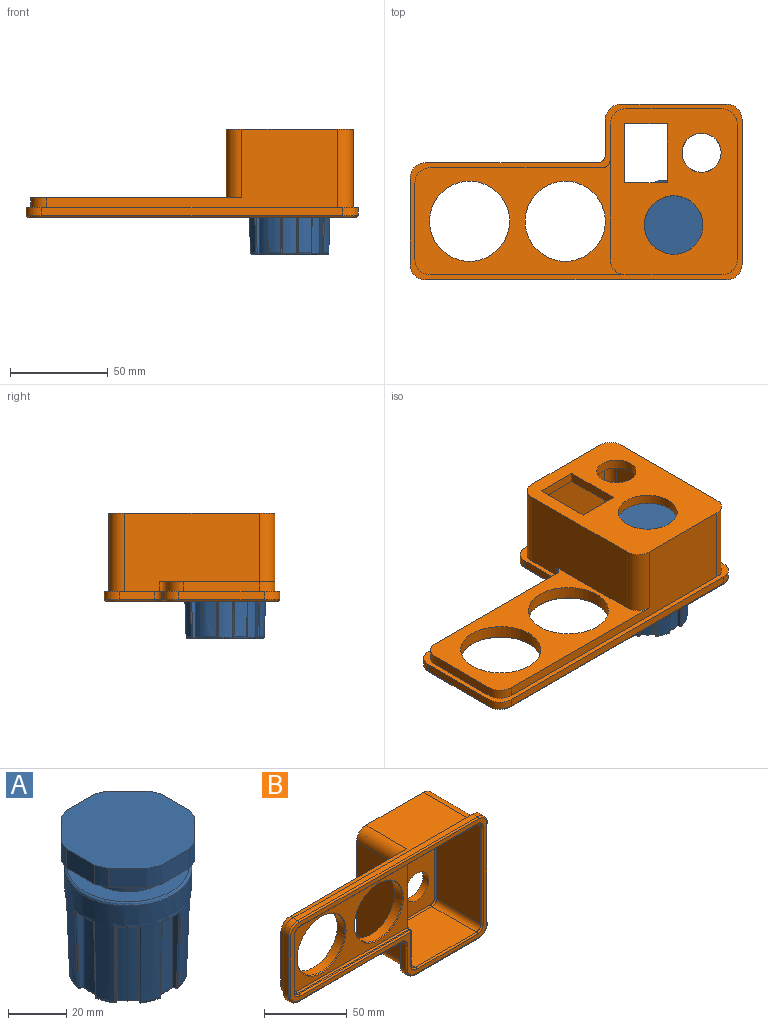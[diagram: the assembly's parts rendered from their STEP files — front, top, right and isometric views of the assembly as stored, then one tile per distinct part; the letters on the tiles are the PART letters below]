
ASSEMBLY  parts=2 mates=1
PART A: 130 faces, bbox 47.5x47.5x84 mm
  f0: cone r=22mm half-angle=2deg, axis (0,0,1), area 3146.3mm2, adj f1,f2,f3,f4,f5,f6,f7,f8
  f1: torus R=19.51mm, axis (0,0,1), area 10.6mm2, adj f0,f20,f72,f123
  f2: torus R=19.51mm, axis (0,0,1), area 10.6mm2, adj f0,f20,f67,f80
  f3: torus R=19.51mm, axis (0,0,1), area 10.6mm2, adj f0,f20,f75,f88
  f4: torus R=19.51mm, axis (0,0,1), area 10.6mm2, adj f0,f20,f83,f96
  f5: torus R=19.51mm, axis (0,0,1), area 10.6mm2, adj f0,f20,f91,f104
  f6: torus R=19.51mm, axis (0,0,1), area 10.6mm2, adj f0,f20,f99,f112
  f7: torus R=19.51mm, axis (0,0,1), area 10.6mm2, adj f0,f20,f107,f120
  f8: torus R=19.51mm, axis (0,0,1), area 10.6mm2, adj f0,f20,f115,f128
  f9: plane 46x46mm, normal (0,0,1), area 1736.1mm2, adj f10,f11,f12,f13,f14,f15,f16,f17
  f10: cylinder r=24mm len=8mm, axis (0,0,1), area 39.6mm2, adj f9,f21,f31,f32
  f11: cylinder r=24mm len=8mm, axis (0,0,1), area 39.6mm2, adj f9,f21,f25,f32
  f12: cylinder r=24mm len=8mm, axis (0,0,1), area 39.6mm2, adj f9,f21,f30,f31
  f13: cylinder r=24mm len=8mm, axis (0,0,1), area 39.6mm2, adj f9,f21,f29,f30
  f14: cylinder r=24mm len=8mm, axis (0,0,1), area 39.6mm2, adj f9,f21,f28,f29
  f15: cylinder r=24mm len=8mm, axis (0,0,1), area 39.6mm2, adj f9,f21,f27,f28
  f16: cylinder r=24mm len=8mm, axis (0,0,1), area 39.6mm2, adj f9,f21,f26,f27
  f17: cylinder r=24mm len=8mm, axis (0,0,1), area 39.6mm2, adj f9,f21,f25,f26
  f18: cylinder r=15mm len=30mm, axis (0,0,1), area 471.2mm2, adj f19,f23
  f19: plane 41.93x41.93mm, normal (0,0,1), area 673.9mm2, adj f18,f24
  f20: plane 38.06x38.06mm, normal (0,0,-1), area 1094.7mm2, adj f1,f2,f3,f4,f5,f6,f7,f8
  f21: plane 46x46mm, normal (0,0,-1), area 350.7mm2, adj f10,f11,f12,f13,f14,f15,f16,f17
  f22: cylinder r=21mm len=42mm, axis (0,0,1), area 197.9mm2, adj f21,f33
  f23: plane 40x40mm, normal (0,0,-1), area 549.8mm2, adj f18,f33
  f24: torus R=20.96mm, axis (0,0,-1), area 218mm2, adj f0,f19
  f25: plane 9.7x9.7mm, normal (0.71,-0.71,0), area 109.7mm2, adj f9,f11,f17,f21
  f26: plane 13.71x8mm, normal (0,-1,0), area 109.7mm2, adj f9,f16,f17,f21
  f27: plane 9.7x9.7mm, normal (-0.71,-0.71,0), area 109.7mm2, adj f9,f15,f16,f21
  f28: plane 13.71x8mm, normal (-1,0,0), area 109.7mm2, adj f9,f14,f15,f21
  f29: plane 9.7x9.7mm, normal (-0.71,0.71,0), area 109.7mm2, adj f9,f13,f14,f21
  f30: plane 13.71x8mm, normal (0,1,0), area 109.7mm2, adj f9,f12,f13,f21
  f31: plane 9.7x9.7mm, normal (0.71,0.71,0), area 109.7mm2, adj f9,f10,f12,f21
  f32: plane 13.71x8mm, normal (1,0,0), area 109.7mm2, adj f9,f10,f11,f21
  f33: cone r=21mm half-angle=45deg, axis (0,0,1), area 182.2mm2, adj f22,f23
  f34: plane 32.5x2.18mm, normal (-0.56,-0.83,0), area 66.7mm2, adj f36,f37,f122,f123,f125
  f35: plane 32.5x2.18mm, normal (0.83,0.56,0), area 66.7mm2, adj f36,f37,f126,f128,f129
  f36: cylinder r=18.5mm len=32.5mm, axis (0,0,-1), area 236.1mm2, adj f34,f35,f37,f127
  f37: plane 7.3x7.3mm, normal (0,0,-1), area 20.6mm2, adj f34,f35,f36,f122,f124,f126
  f38: plane 32.5x2.57mm, normal (-0.98,-0.2,0), area 66.7mm2, adj f40,f41,f114,f115,f117
  f39: plane 32.5x2.57mm, normal (0.98,-0.2,0), area 66.7mm2, adj f40,f41,f118,f120,f121
  f40: cylinder r=18.5mm len=32.5mm, axis (0,0,-1), area 236.1mm2, adj f38,f39,f41,f119
  f41: plane 8.25x3mm, normal (0,0,-1), area 20.6mm2, adj f38,f39,f40,f114,f116,f118
  f42: plane 32.5x2.18mm, normal (-0.83,0.56,0), area 66.7mm2, adj f44,f45,f106,f107,f109
  f43: plane 32.5x2.18mm, normal (0.56,-0.83,0), area 66.7mm2, adj f44,f45,f110,f112,f113
  f44: cylinder r=18.5mm len=32.5mm, axis (0,0,-1), area 236.1mm2, adj f42,f43,f45,f111
  f45: plane 7.3x7.3mm, normal (0,0,-1), area 20.6mm2, adj f42,f43,f44,f106,f108,f110
  f46: plane 32.5x2.57mm, normal (-0.2,0.98,0), area 66.7mm2, adj f48,f49,f98,f99,f101
  f47: plane 32.5x2.57mm, normal (-0.2,-0.98,0), area 66.7mm2, adj f48,f49,f102,f104,f105
  f48: cylinder r=18.5mm len=32.5mm, axis (0,0,-1), area 236.1mm2, adj f46,f47,f49,f103
  f49: plane 8.25x3mm, normal (0,0,-1), area 20.6mm2, adj f46,f47,f48,f98,f100,f102
  f50: plane 32.5x2.18mm, normal (0.56,0.83,0), area 66.7mm2, adj f52,f53,f90,f91,f93
  f51: plane 32.5x2.18mm, normal (-0.83,-0.56,0), area 66.7mm2, adj f52,f53,f94,f96,f97
  f52: cylinder r=18.5mm len=32.5mm, axis (0,0,-1), area 236.1mm2, adj f50,f51,f53,f95
  f53: plane 7.3x7.3mm, normal (0,0,-1), area 20.6mm2, adj f50,f51,f52,f90,f92,f94
  f54: plane 32.5x2.57mm, normal (0.98,0.2,0), area 66.7mm2, adj f56,f57,f82,f83,f85
  f55: plane 32.5x2.57mm, normal (-0.98,0.2,0), area 66.7mm2, adj f56,f57,f86,f88,f89
  f56: cylinder r=18.5mm len=32.5mm, axis (0,0,-1), area 236.1mm2, adj f54,f55,f57,f87
  f57: plane 8.25x3mm, normal (0,0,-1), area 20.6mm2, adj f54,f55,f56,f82,f84,f86
  f58: plane 32.5x2.18mm, normal (0.83,-0.56,0), area 66.7mm2, adj f60,f61,f74,f75,f77
  f59: plane 32.5x2.18mm, normal (-0.56,0.83,0), area 66.7mm2, adj f60,f61,f78,f80,f81
  f60: cylinder r=18.5mm len=32.5mm, axis (0,0,-1), area 236.1mm2, adj f58,f59,f61,f79
  f61: plane 7.3x7.3mm, normal (0,0,-1), area 20.6mm2, adj f58,f59,f60,f74,f76,f78
  f62: plane 8.25x3mm, normal (0,0,-1), area 20.6mm2, adj f63,f64,f65,f66,f68,f70
  f63: plane 32.5x2.57mm, normal (0.2,0.98,0), area 66.7mm2, adj f62,f64,f70,f72,f73
  f64: cylinder r=18.5mm len=32.5mm, axis (0,0,-1), area 236.1mm2, adj f62,f63,f65,f71
  f65: plane 32.5x2.57mm, normal (0.2,-0.98,0), area 66.7mm2, adj f62,f64,f66,f67,f69
  f66: bspline ~64.42x2.71mm, area 25.7mm2, adj f0,f62,f65,f67,f68
  f67: bspline ~1.19x1.15mm, area 1mm2, adj f2,f65,f66,f69
  f68: torus R=21.14mm, axis (0,0,-1), area 6.9mm2, adj f0,f62,f66,f70
  f69: cylinder r=0.5mm len=1.58mm, axis (0.98,0.2,0), area 1mm2, adj f20,f65,f67,f71
  f70: bspline ~64.42x2.71mm, area 25.7mm2, adj f0,f62,f63,f68,f72
  f71: torus R=18mm, axis (0,0,1), area 6mm2, adj f20,f64,f69,f73
  f72: bspline ~1.31x1.19mm, area 1mm2, adj f1,f63,f70,f73
  f73: cylinder r=0.5mm len=1.58mm, axis (-0.98,0.2,0), area 1mm2, adj f20,f63,f71,f72
  f74: bspline ~64.42x2.57mm, area 25.7mm2, adj f0,f58,f61,f75,f76
  f75: bspline ~1.3x1.19mm, area 1mm2, adj f3,f58,f74,f77
  f76: torus R=21.14mm, axis (0,0,-1), area 6.9mm2, adj f0,f61,f74,f78
  f77: cylinder r=0.5mm len=1.53mm, axis (0.56,0.83,0), area 1mm2, adj f20,f58,f75,f79
  f78: bspline ~64.42x2.57mm, area 25.7mm2, adj f0,f59,f61,f76,f80
  f79: torus R=18mm, axis (0,0,1), area 6mm2, adj f20,f60,f77,f81
  f80: bspline ~1.3x1.19mm, area 1mm2, adj f2,f59,f78,f81
  f81: cylinder r=0.5mm len=1.53mm, axis (-0.83,-0.56,0), area 1mm2, adj f20,f59,f79,f80
  f82: bspline ~64.42x2.71mm, area 25.7mm2, adj f0,f54,f57,f83,f84
  f83: bspline ~1.19x1.15mm, area 1mm2, adj f4,f54,f82,f85
  f84: torus R=21.14mm, axis (0,0,-1), area 6.9mm2, adj f0,f57,f82,f86
  f85: cylinder r=0.5mm len=1.58mm, axis (-0.2,0.98,0), area 1mm2, adj f20,f54,f83,f87
  f86: bspline ~64.42x2.71mm, area 25.7mm2, adj f0,f55,f57,f84,f88
  f87: torus R=18mm, axis (0,0,1), area 6mm2, adj f20,f56,f85,f89
  f88: bspline ~1.31x1.19mm, area 1mm2, adj f3,f55,f86,f89
  f89: cylinder r=0.5mm len=1.58mm, axis (-0.2,-0.98,0), area 1mm2, adj f20,f55,f87,f88
  f90: bspline ~64.42x2.57mm, area 25.7mm2, adj f0,f50,f53,f91,f92
  f91: bspline ~1.19x1.16mm, area 1mm2, adj f5,f50,f90,f93
  f92: torus R=21.14mm, axis (0,0,-1), area 6.9mm2, adj f0,f53,f90,f94
  f93: cylinder r=0.5mm len=1.53mm, axis (-0.83,0.56,0), area 1mm2, adj f20,f50,f91,f95
  f94: bspline ~64.42x2.57mm, area 25.7mm2, adj f0,f51,f53,f92,f96
  f95: torus R=18mm, axis (0,0,1), area 6mm2, adj f20,f52,f93,f97
  f96: bspline ~1.3x1.19mm, area 1mm2, adj f4,f51,f94,f97
  f97: cylinder r=0.5mm len=1.53mm, axis (0.56,-0.83,0), area 1mm2, adj f20,f51,f95,f96
  f98: bspline ~64.42x2.71mm, area 25.7mm2, adj f0,f46,f49,f99,f100
  f99: bspline ~1.19x1.15mm, area 1mm2, adj f6,f46,f98,f101
  f100: torus R=21.14mm, axis (0,0,-1), area 6.9mm2, adj f0,f49,f98,f102
  f101: cylinder r=0.5mm len=1.58mm, axis (-0.98,-0.2,0), area 1mm2, adj f20,f46,f99,f103
  f102: bspline ~64.42x2.71mm, area 25.7mm2, adj f0,f47,f49,f100,f104
  f103: torus R=18mm, axis (0,0,1), area 6mm2, adj f20,f48,f101,f105
  f104: bspline ~1.31x1.19mm, area 1mm2, adj f5,f47,f102,f105
  f105: cylinder r=0.5mm len=1.58mm, axis (0.98,-0.2,0), area 1mm2, adj f20,f47,f103,f104
  f106: bspline ~64.42x2.57mm, area 25.7mm2, adj f0,f42,f45,f107,f108
  f107: bspline ~1.19x1.16mm, area 1mm2, adj f7,f42,f106,f109
  f108: torus R=21.14mm, axis (0,0,-1), area 6.9mm2, adj f0,f45,f106,f110
  f109: cylinder r=0.5mm len=1.53mm, axis (-0.56,-0.83,0), area 1mm2, adj f20,f42,f107,f111
  f110: bspline ~64.42x2.57mm, area 25.7mm2, adj f0,f43,f45,f108,f112
  f111: torus R=18mm, axis (0,0,1), area 6mm2, adj f20,f44,f109,f113
  f112: bspline ~1.3x1.19mm, area 1mm2, adj f6,f43,f110,f113
  f113: cylinder r=0.5mm len=1.53mm, axis (0.83,0.56,0), area 1mm2, adj f20,f43,f111,f112
  f114: bspline ~64.42x2.71mm, area 25.7mm2, adj f0,f38,f41,f115,f116
  f115: bspline ~1.19x1.15mm, area 1mm2, adj f8,f38,f114,f117
  f116: torus R=21.14mm, axis (0,0,-1), area 6.9mm2, adj f0,f41,f114,f118
  f117: cylinder r=0.5mm len=1.58mm, axis (0.2,-0.98,0), area 1mm2, adj f20,f38,f115,f119
  f118: bspline ~64.42x2.71mm, area 25.7mm2, adj f0,f39,f41,f116,f120
  f119: torus R=18mm, axis (0,0,1), area 6mm2, adj f20,f40,f117,f121
  f120: bspline ~1.31x1.19mm, area 1mm2, adj f7,f39,f118,f121
  f121: cylinder r=0.5mm len=1.58mm, axis (0.2,0.98,0), area 1mm2, adj f20,f39,f119,f120
  f122: bspline ~64.42x2.57mm, area 25.7mm2, adj f0,f34,f37,f123,f124
  f123: bspline ~1.19x1.16mm, area 1mm2, adj f1,f34,f122,f125
  f124: torus R=21.14mm, axis (0,0,-1), area 6.9mm2, adj f0,f37,f122,f126
  f125: cylinder r=0.5mm len=1.53mm, axis (0.83,-0.56,0), area 1mm2, adj f20,f34,f123,f127
  f126: bspline ~64.42x2.57mm, area 25.7mm2, adj f0,f35,f37,f124,f128
  f127: torus R=18mm, axis (0,0,1), area 6mm2, adj f20,f36,f125,f129
  f128: bspline ~1.3x1.19mm, area 1mm2, adj f8,f35,f126,f129
  f129: cylinder r=0.5mm len=1.53mm, axis (-0.56,0.83,0), area 1mm2, adj f20,f35,f127,f128
PART B: 94 faces, bbox 171.3x45x91.3 mm
  f0: plane 85x65.02mm, normal (0,1,0), area 3786.4mm2, adj f4,f21,f22,f23,f37,f38,f39,f41
  f1: plane 78x58mm, normal (0,-1,0), area 2832.8mm2, adj f42,f43,f44,f45,f46,f47,f48,f88
  f2: plane 98x48mm, normal (0,-1,0), area 1929.3mm2, adj f49,f51,f52,f56,f60,f61,f86,f87
  f3: plane 107.98x59mm, normal (0,1,0), area 2848.1mm2, adj f4,f5,f6,f21,f35,f36,f40,f41
  f4: plane 149x40mm, normal (0,0,1), area 2460.7mm2, adj f0,f3,f20,f36,f37,f41
  f5: plane 39x5mm, normal (-1,0,0), area 195mm2, adj f3,f20,f35,f36
  f6: plane 87.98x5mm, normal (0,0,-1), area 439.9mm2, adj f3,f20,f35,f40
  f7: plane 72x38mm, normal (-1,0,0), area 2736mm2, adj f30,f34,f43,f62
  f8: plane 52x38mm, normal (0,0,1), area 1976mm2, adj f30,f31,f44,f68
  f9: plane 75x38mm, normal (1,0,0), area 2700.9mm2, adj f31,f48,f53,f61,f64,f67,f71
  f10: plane 95x1mm, normal (0,0,1), area 95mm2, adj f32,f60,f66,f67
  f11: plane 42x1mm, normal (1,0,0), area 42mm2, adj f32,f33,f51,f59
  f12: plane 74x4mm, normal (1,0,0), area 296mm2, adj f20,f24,f28,f75
  f13: plane 154x4mm, normal (0,0,1), area 616mm2, adj f20,f24,f25,f72
  f14: plane 44x4mm, normal (-1,0,0), area 176mm2, adj f20,f25,f26,f76
  f15: plane 88x4mm, normal (0,0,-1), area 352mm2, adj f20,f26,f29,f80
  f16: plane 18x4mm, normal (-1,0,0), area 72mm2, adj f20,f27,f29,f83
  f17: plane 54x4mm, normal (0,0,-1), area 216mm2, adj f20,f27,f28,f79
  f18: plane 152x38mm, normal (0,0,-1), area 2187.9mm2, adj f33,f34,f47,f52,f53,f54,f57
  f19: plane 168x88mm, normal (0,-1,0), area 1479.6mm2, adj f54,f55,f58,f59,f62,f63,f65,f66
  f20: plane 170x90mm, normal (0,1,0), area 1274.4mm2, adj f4,f5,f6,f12,f13,f14,f15,f16
  f21: plane 69x40mm, normal (-1,0,0), area 2505mm2, adj f0,f3,f20,f39,f40,f41
  f22: plane 49.02x40mm, normal (0,0,-1), area 1960.8mm2, adj f0,f20,f38,f39
  f23: plane 69x40mm, normal (1,0,0), area 2760mm2, adj f0,f20,f37,f38
  f24: cylinder r=8mm len=8mm, axis (0,-1,0), area 50.3mm2, adj f12,f13,f20,f73
  f25: cylinder r=8mm len=8mm, axis (0,1,0), area 50.3mm2, adj f13,f14,f20,f74
  f26: cylinder r=8mm len=8mm, axis (0,1,0), area 50.3mm2, adj f14,f15,f20,f78
  f27: cylinder r=8mm len=8mm, axis (0,1,0), area 50.3mm2, adj f16,f17,f20,f81
  f28: cylinder r=8mm len=8mm, axis (0,1,0), area 50.3mm2, adj f12,f17,f20,f77
  f29: cylinder r=4mm len=4mm, axis (0,1,0), area 25.1mm2, adj f15,f16,f20,f82
  f30: cylinder r=4mm len=38mm, axis (0,-1,0), area 238.8mm2, adj f7,f8,f42,f65
  f31: cylinder r=4mm len=38mm, axis (0,-1,0), area 238.8mm2, adj f8,f9,f46,f70
  f32: cylinder r=4mm len=4mm, axis (0,1,0), area 6.3mm2, adj f10,f11,f56,f63
  f33: cylinder r=4mm len=4mm, axis (0,-1,0), area 6.3mm2, adj f11,f18,f49,f55
  f34: cylinder r=4mm len=38mm, axis (0,1,0), area 238.8mm2, adj f7,f18,f45,f58
  f35: cylinder r=8mm len=8mm, axis (0,1,0), area 62.8mm2, adj f3,f5,f6,f20
  f36: cylinder r=8mm len=8mm, axis (0,-1,0), area 62.8mm2, adj f3,f4,f5,f20
  f37: cylinder r=8mm len=40mm, axis (0,1,0), area 502.7mm2, adj f0,f4,f20,f23
  f38: cylinder r=8mm len=40mm, axis (0,-1,0), area 502.7mm2, adj f0,f20,f22,f23
  f39: cylinder r=8mm len=40mm, axis (0,1,0), area 502.7mm2, adj f0,f20,f21,f22
  f40: cylinder r=4mm len=5mm, axis (0,-1,0), area 31.4mm2, adj f3,f6,f20,f21
  f41: cylinder r=8mm len=35mm, axis (0,1,0), area 439.8mm2, adj f0,f3,f4,f21
  f42: torus R=3mm, axis (0,-1,0), area 9mm2, adj f1,f30,f43,f44
  f43: cylinder r=1mm len=72mm, axis (0,0,-1), area 113.1mm2, adj f1,f7,f42,f45
  f44: cylinder r=1mm len=52mm, axis (-1,0,0), area 81.7mm2, adj f1,f8,f42,f46
  f45: torus R=3mm, axis (0,-1,0), area 9mm2, adj f1,f34,f43,f47
  f46: torus R=3mm, axis (0,-1,0), area 9mm2, adj f1,f31,f44,f48
  f47: cylinder r=1mm len=55mm, axis (1,0,0), area 86.4mm2, adj f1,f18,f45,f50
  f48: cylinder r=1mm len=75mm, axis (0,0,-1), area 117.8mm2, adj f1,f9,f46,f50
  f49: torus R=3mm, axis (0,1,0), area 9mm2, adj f2,f33,f51,f52
  f50: sphere r=1mm, area 1.6mm2, adj f47,f48,f53
  f51: cylinder r=1mm len=42mm, axis (0,0,-1), area 66mm2, adj f2,f11,f49,f56
  f52: cylinder r=1mm len=95mm, axis (-1,0,0), area 149.2mm2, adj f2,f18,f49,f57
  f53: cylinder r=1mm len=35mm, axis (0,-1,0), area 55mm2, adj f9,f18,f50,f57
  f54: cylinder r=1mm len=152mm, axis (-1,0,0), area 238.8mm2, adj f18,f19,f55,f58
  f55: torus R=5mm, axis (0,-1,0), area 10.8mm2, adj f19,f33,f54,f59
  f56: torus R=3mm, axis (0,1,0), area 9mm2, adj f2,f32,f51,f60
  f57: torus R=2mm, axis (0,0,1), area 3.4mm2, adj f18,f52,f53,f61
  f58: torus R=5mm, axis (0,-1,0), area 10.8mm2, adj f19,f34,f54,f62
  f59: cylinder r=1mm len=42mm, axis (0,0,-1), area 66mm2, adj f11,f19,f55,f63
  f60: cylinder r=1mm len=95mm, axis (1,0,0), area 149.2mm2, adj f2,f10,f56,f64
  f61: cylinder r=1mm len=48mm, axis (0,0,-1), area 75.4mm2, adj f2,f9,f57,f64
  f62: cylinder r=1mm len=72mm, axis (0,0,1), area 113.1mm2, adj f7,f19,f58,f65
  f63: torus R=5mm, axis (0,-1,0), area 10.8mm2, adj f19,f32,f59,f66
  f64: torus R=2mm, axis (1,0,0), area 3.4mm2, adj f9,f60,f61,f67
  f65: torus R=5mm, axis (0,-1,0), area 10.8mm2, adj f19,f30,f62,f68
  f66: cylinder r=1mm len=95mm, axis (1,0,0), area 149.2mm2, adj f10,f19,f63,f69
  f67: cylinder r=1mm len=1mm, axis (0,1,0), area 1.6mm2, adj f9,f10,f64,f69
  f68: cylinder r=1mm len=52mm, axis (1,0,0), area 81.7mm2, adj f8,f19,f65,f70
  f69: sphere r=1mm, area 1.6mm2, adj f66,f67,f71
  f70: torus R=5mm, axis (0,-1,0), area 10.8mm2, adj f19,f31,f68,f71
  f71: cylinder r=1mm len=25mm, axis (0,0,-1), area 39.3mm2, adj f9,f19,f69,f70
  f72: cylinder r=1mm len=154mm, axis (1,0,0), area 241.9mm2, adj f13,f19,f73,f74
  f73: torus R=7mm, axis (0,-1,0), area 18.8mm2, adj f19,f24,f72,f75
  f74: torus R=7mm, axis (0,-1,0), area 18.8mm2, adj f19,f25,f72,f76
  f75: cylinder r=1mm len=74mm, axis (0,0,-1), area 116.2mm2, adj f12,f19,f73,f77
  f76: cylinder r=1mm len=44mm, axis (0,0,1), area 69.1mm2, adj f14,f19,f74,f78
  f77: torus R=7mm, axis (0,-1,0), area 18.8mm2, adj f19,f28,f75,f79
  f78: torus R=7mm, axis (0,-1,0), area 18.8mm2, adj f19,f26,f76,f80
  f79: cylinder r=1mm len=54mm, axis (-1,0,0), area 84.8mm2, adj f17,f19,f77,f81
  f80: cylinder r=1mm len=88mm, axis (-1,0,0), area 138.2mm2, adj f15,f19,f78,f82
  f81: torus R=7mm, axis (0,-1,0), area 18.8mm2, adj f19,f27,f79,f83
  f82: torus R=5mm, axis (0,-1,0), area 10.8mm2, adj f19,f29,f80,f83
  f83: cylinder r=1mm len=18mm, axis (0,0,1), area 28.3mm2, adj f16,f19,f81,f82
  f84: cylinder r=20.5mm len=41mm, axis (0,-1,0), area 837.2mm2, adj f3,f86
  f85: cylinder r=20.5mm len=41mm, axis (0,-1,0), area 837.2mm2, adj f3,f87
  f86: cone r=21mm half-angle=45deg, axis (0,-1,0), area 92.2mm2, adj f2,f84
  f87: cone r=20.5mm half-angle=45deg, axis (0,-1,0), area 92.2mm2, adj f2,f85
  f88: cylinder r=10mm len=20mm, axis (0,-1,0), area 314.2mm2, adj f0,f1
  f89: plane 22x5mm, normal (0,0,1), area 110mm2, adj f0,f1,f90,f92
  f90: plane 30.2x5mm, normal (-1,0,0), area 151mm2, adj f0,f1,f89,f91
  f91: plane 22x5mm, normal (0,0,-1), area 110mm2, adj f0,f1,f90,f92
  f92: plane 30.2x5mm, normal (1,0,0), area 151mm2, adj f0,f1,f89,f91
  f93: cylinder r=15mm len=30mm, axis (0,-1,0), area 471.2mm2, adj f0,f1
PLACE A t=(9.09,-8.9,8.41)mm
PLACE B rot(axis=(1,0,0),90deg) t=(-40.91,8.1,-26.59)mm
MATE fastened B.f93 <-> A.f0  axis (0,0,-1) through (9.09,-8.9,8.41)mm
